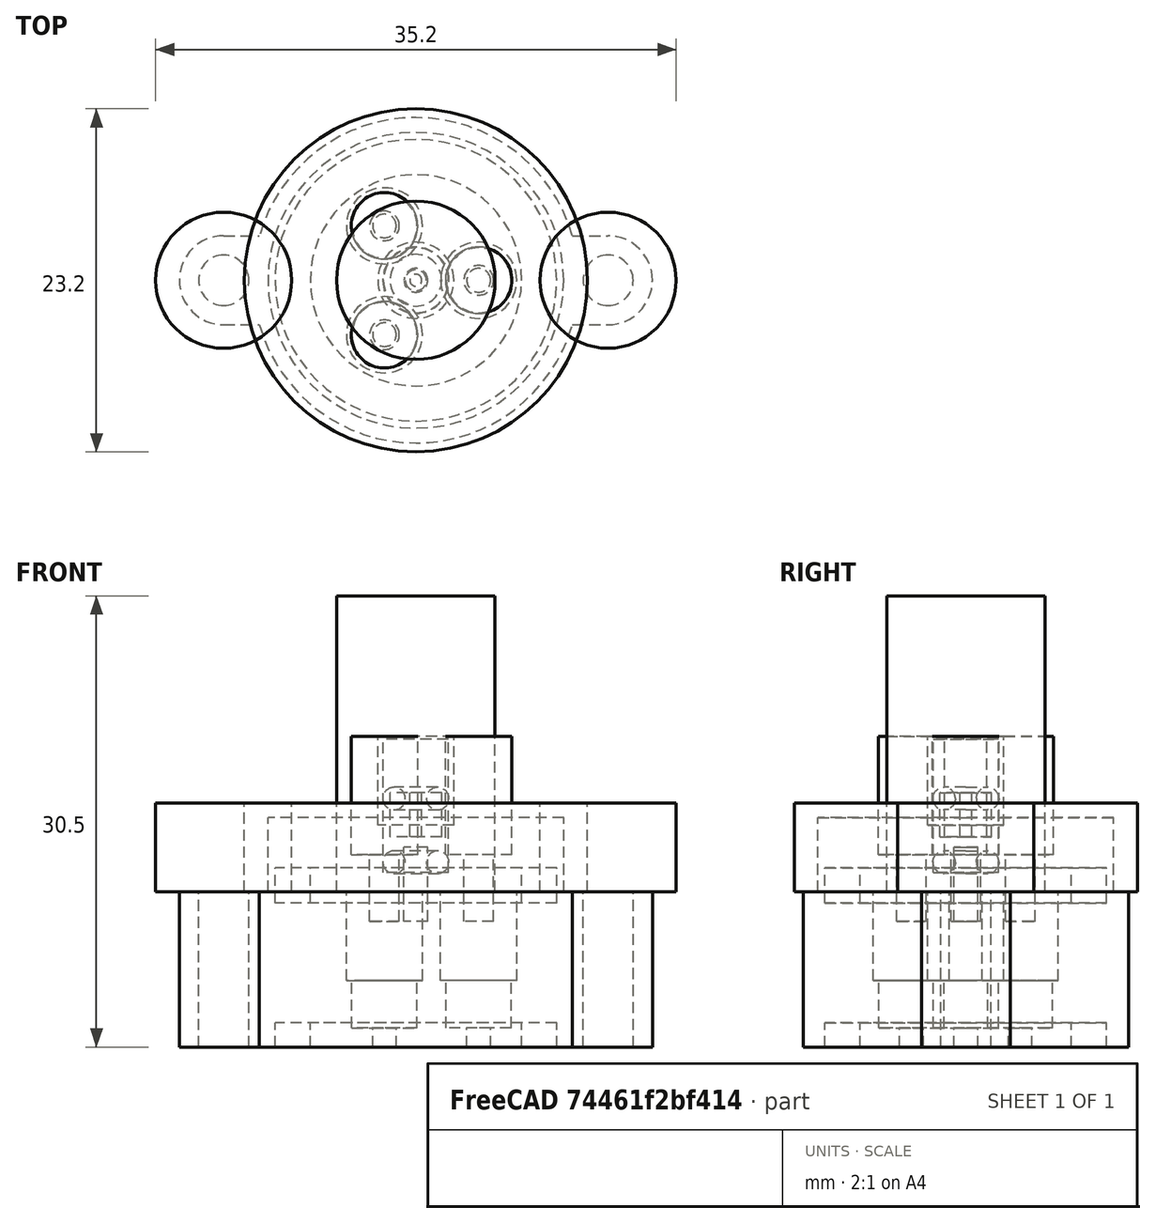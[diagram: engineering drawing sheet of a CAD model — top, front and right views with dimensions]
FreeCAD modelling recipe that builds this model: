
FCSTD DOCUMENT  (FreeCAD 0.17R13509 (Git))
Label: ceramic_wire_feedthroughs_insert
License: All rights reserved
LicenseURL: http://en.wikipedia.org/wiki/All_rights_reserved
objects: Part::Cylinder×45, Part::MultiFuse×10, Part::Cut×8, Part::Box×6, Part::FeaturePython×4, Part::Feature×2, App::FeaturePython×1
note: 75 computed .brp shape members not serialized (recipe doc carries the construction recipe); baked Part::Feature solids carry a one-line shape summary decoded from their .brp

FEATURE [Part::Cylinder] Cylinder155  label="Cylinder009"
  Angle = 360
  AttacherType = Attacher::AttachEngine3D
  Height = 2.38125
  Radius = 9.525
  expr: Radius = 3 / 4 * 25.399999999999999 / 2
  expr: Height = 3 / 32 * 25.399999999999999
FEATURE [Part::Cylinder] Cylinder154  label="Cylinder008"
  Angle = 360
  AttacherType = Attacher::AttachEngine3D
  Height = 2.38125
  Radius = 7.14375
  expr: Radius = 9 / 16 * 25.399999999999999 / 2
  expr: Height = 3 / 32 * 25.399999999999999
FEATURE [Part::Feature] Part__Feature001  label="TopOring"
  Placement = pos=(0,0,6.3) rot=(0,0,1;0rad)
  shape: bbox 4.839 x 4.839 x 1.524 mm, 4 faces (baked)
FEATURE [Part::Feature] Part__Feature002  label="BottomOring"
  Placement = pos=(0,0,2) rot=(0,0,1;0rad)
  shape: bbox 4.839 x 4.839 x 1.524 mm, 4 faces (baked)
FEATURE [Part::Cylinder] Cylinder153  label="Body"
  Angle = 360
  AttacherType = Attacher::AttachEngine3D
  Height = 5
  Radius = 10
FEATURE [Part::Cut] Cut019  label="Oring"
  Base = -> Cylinder155
  Placement = pos=(0,0,-0.75) rot=(0,0,1;0rad)
  Tool = -> Cylinder154
FEATURE [Part::Cylinder] Cylinder147  label="ThreadedSection"
  Angle = 360
  AttacherType = Attacher::AttachEngine3D
  Height = 1
  Placement = pos=(0,0,4.5) rot=(0,0,1;0rad)
  Radius = 1
FEATURE [Part::Cylinder] Cylinder149  label="FTBead"
  Angle = 360
  AttacherType = Attacher::AttachEngine3D
  Height = 3
  Placement = pos=(0,0,2.7) rot=(0,0,1;0rad)
  Radius = 1.75
  expr: Radius = 3.5 / 2
FEATURE [Part::Cylinder] Cylinder152  label="RFFeeds005"
  Angle = 360
  AttacherType = Attacher::AttachEngine3D
  Height = 20
  Radius = 5.35813
  expr: Placement.Base.x = 0
FEATURE [Part::Cylinder] Cylinder156  label="BottomWireOutlet"
  Angle = 360
  AttacherType = Attacher::AttachEngine3D
  Height = 5
  Placement = pos=(0,0,-2) rot=(0,0,1;0rad)
  Radius = 1
FEATURE [Part::Cylinder] Cylinder157  label="SealSubtraction"
  Angle = 360
  AttacherType = Attacher::AttachEngine3D
  Height = 8
  Placement = pos=(0,0,2.5) rot=(0,0,1;0rad)
  Radius = 2.25
FEATURE [Part::MultiFuse] Fusion
  Placement = pos=(4.25,0,0) rot=(0,0,1;0rad)
  Shapes = -> [Cylinder147,Cylinder157,Cylinder156]
FEATURE [Part::FeaturePython] Array  label="SealArray"  # Draft array (typed FeaturePython)
  Angle = 360
  ArrayType = 1
  Axis = (0,0,1)
  Base = -> Fusion
  Center = (0,0,0)
  Fuse = false
  IntervalAxis = (0,0,0)
  IntervalX = (1,0,0)
  IntervalY = (0,1,0)
  IntervalZ = (0,0,0)
  NumberPolar = 3
  NumberX = 2
  NumberY = 2
  NumberZ = 1
FEATURE [Part::Cylinder] Cylinder159  label="FTBeadHole"
  Angle = 360
  AttacherType = Attacher::AttachEngine3D
  Height = 17
  Radius = 0.405
  expr: Radius = 0.81000000000000005 / 2
FEATURE [Part::Cut] Cut020
  Base = -> Cylinder149
  Placement = pos=(0,0,1) rot=(0,0,1;0rad)
  Tool = -> Cylinder159
FEATURE [Part::Cylinder] Cylinder160  label="Cylinder010"
  Angle = 360
  AttacherType = Attacher::AttachEngine3D
  Height = 2.38125
  Radius = 9.525
  expr: Radius = 3 / 4 * 25.399999999999999 / 2
  expr: Height = 3 / 32 * 25.399999999999999
FEATURE [Part::Cylinder] Cylinder161  label="WireFeedsMount003"
  Angle = 360
  AttacherType = Attacher::AttachEngine3D
  Height = 11
  Placement = pos=(-13,0,0) rot=(0,0,1;0rad)
  Radius = 1.7
FEATURE [Part::Cylinder] Cylinder162  label="ThreadedSection001"
  Angle = 360
  AttacherType = Attacher::AttachEngine3D
  Height = 6
  Placement = pos=(0,0,4.5) rot=(0,0,1;0rad)
  Radius = 2.575
  expr: Radius = 5.1500000000000004 / 2
FEATURE [Part::Cylinder] Cylinder163  label="Cylinder011"
  Angle = 360
  AttacherType = Attacher::AttachEngine3D
  Height = 2.38125
  Radius = 7.14375
  expr: Radius = 9 / 16 * 25.399999999999999 / 2
  expr: Height = 3 / 32 * 25.399999999999999
FEATURE [Part::Cut] Cut022  label="Oring001"
  Base = -> Cylinder160
  Placement = pos=(0,0,-0.75) rot=(0,0,1;0rad)
  Tool = -> Cylinder163
FEATURE [Part::Cylinder] Cylinder164  label="Body001"
  Angle = 360
  AttacherType = Attacher::AttachEngine3D
  Height = 10.5
  Radius = 11
FEATURE [Part::Cylinder] Cylinder165  label="WireFeedsMount004"
  Angle = 360
  AttacherType = Attacher::AttachEngine3D
  Height = 11
  Placement = pos=(13,0,0) rot=(0,0,1;0rad)
  Radius = 1.7
FEATURE [Part::Cylinder] Cylinder166  label="BottomWireOutlet001"
  Angle = 360
  AttacherType = Attacher::AttachEngine3D
  Height = 5
  Placement = pos=(0,0,-2) rot=(0,0,1;0rad)
  Radius = 0.8
FEATURE [Part::Cylinder] Cylinder167  label="SealSubtraction001"
  Angle = 360
  AttacherType = Attacher::AttachEngine3D
  Height = 9
  Placement = pos=(0,0,1.3) rot=(0,0,1;0rad)
  Radius = 2.2
FEATURE [Part::Box] Box002  label="MountCube003"
  AttacherType = Attacher::AttachEngine3D
  Height = 10.5
  Length = 3
  Placement = pos=(10,-3,0) rot=(0,0,1;0rad)
  Width = 6
FEATURE [Part::Box] Box003  label="MountCube004"
  AttacherType = Attacher::AttachEngine3D
  Height = 10.5
  Length = 3
  Placement = pos=(-13,-3,0) rot=(0,0,1;0rad)
  Width = 6
FEATURE [Part::MultiFuse] Fusion004
  Placement = pos=(4.25,0,0) rot=(0,0,1;0rad)
  Shapes = -> [Cylinder162,Cylinder167,Cylinder166]
FEATURE [Part::Cylinder] Cylinder168  label="MountFlange003"
  Angle = 360
  AttacherType = Attacher::AttachEngine3D
  Height = 10.5
  Placement = pos=(-13,0,0) rot=(0,0,1;0rad)
  Radius = 3
FEATURE [Part::Cylinder] Cylinder169  label="MountFlange004"
  Angle = 360
  AttacherType = Attacher::AttachEngine3D
  Height = 10.5
  Placement = pos=(13,0,0) rot=(0,0,1;0rad)
  Radius = 3
FEATURE [Part::MultiFuse] Fusion003
  Shapes = -> [Cylinder169,Box002,Box003,Cylinder168,Cylinder164]
FEATURE [Part::FeaturePython] Array001  label="SealArray001"  # Draft array (typed FeaturePython)
  Angle = 360
  ArrayType = 1
  Axis = (0,0,1)
  Base = -> Fusion004
  Center = (0,0,0)
  Fuse = false
  IntervalAxis = (0,0,0)
  IntervalX = (1,0,0)
  IntervalY = (0,1,0)
  IntervalZ = (0,0,0)
  NumberPolar = 3
  NumberX = 2
  NumberY = 2
  NumberZ = 1
FEATURE [Part::MultiFuse] Fusion005
  Shapes = -> [Cylinder165,Cylinder161,Cut022,Array001]
FEATURE [Part::Cut] Cut021
  Base = -> Fusion003
  Placement = pos=(0,0,-10.5) rot=(0,0,1;0rad)
  Tool = -> Fusion005
FEATURE [Part::Cylinder] Cylinder170  label="Cylinder012"
  Angle = 360
  AttacherType = Attacher::AttachEngine3D
  Height = 2.38125
  Radius = 9.525
  expr: Radius = 3 / 4 * 25.399999999999999 / 2
  expr: Height = 3 / 32 * 25.399999999999999
FEATURE [Part::Cylinder] Cylinder171  label="WireFeedsMount005"
  Angle = 360
  AttacherType = Attacher::AttachEngine3D
  Height = 11
  Placement = pos=(-13,0,0) rot=(0,0,1;0rad)
  Radius = 1.7
FEATURE [Part::Cylinder] Cylinder172  label="ThreadedSection002"
  Angle = 360
  AttacherType = Attacher::AttachEngine3D
  Height = 6
  Placement = pos=(0,0,4.5) rot=(0,0,1;0rad)
  Radius = 2.575
  expr: Radius = 5.1500000000000004 / 2
FEATURE [Part::Cylinder] Cylinder173  label="Cylinder013"
  Angle = 360
  AttacherType = Attacher::AttachEngine3D
  Height = 2.38125
  Radius = 7.14375
  expr: Radius = 9 / 16 * 25.399999999999999 / 2
  expr: Height = 3 / 32 * 25.399999999999999
FEATURE [Part::Cut] Cut024  label="Oring002"
  Base = -> Cylinder170
  Placement = pos=(0,0,-0.75) rot=(0,0,1;0rad)
  Tool = -> Cylinder173
FEATURE [Part::Cylinder] Cylinder174  label="Body002"
  Angle = 360
  AttacherType = Attacher::AttachEngine3D
  Height = 10.5
  Radius = 11
FEATURE [Part::Cylinder] Cylinder175  label="WireFeedsMount006"
  Angle = 360
  AttacherType = Attacher::AttachEngine3D
  Height = 11
  Placement = pos=(13,0,0) rot=(0,0,1;0rad)
  Radius = 1.7
FEATURE [Part::Cylinder] Cylinder176  label="BottomWireOutlet002"
  Angle = 360
  AttacherType = Attacher::AttachEngine3D
  Height = 5
  Placement = pos=(0,0,-2) rot=(0,0,1;0rad)
  Radius = 0.8
FEATURE [Part::Cylinder] Cylinder177  label="SealSubtraction002"
  Angle = 360
  AttacherType = Attacher::AttachEngine3D
  Height = 9
  Placement = pos=(0,0,1.3) rot=(0,0,1;0rad)
  Radius = 2.2
FEATURE [Part::Box] Box004  label="MountCube005"
  AttacherType = Attacher::AttachEngine3D
  Height = 10.5
  Length = 3
  Placement = pos=(10,-3,0) rot=(0,0,1;0rad)
  Width = 6
FEATURE [App::FeaturePython] SetupSheet002  # Path/CAM operation (typed FeaturePython)
  ClearanceHeightExpression = StartDepth+SetupSheet.ClearanceHeightOffset
  ClearanceHeightOffset = 5
  FinalDepthExpression = OpFinalDepth
  HorizRapid = 0
  SafeHeightExpression = StartDepth+SetupSheet.SafeHeightOffset
  SafeHeightOffset = 3
  StartDepthExpression = OpStartDepth
  StepDownExpression = OpToolDiameter
  VertRapid = 0
FEATURE [Part::Box] Box005  label="MountCube006"
  AttacherType = Attacher::AttachEngine3D
  Height = 10.5
  Length = 3
  Placement = pos=(-13,-3,0) rot=(0,0,1;0rad)
  Width = 6
FEATURE [Part::MultiFuse] Fusion007
  Placement = pos=(4.25,0,0) rot=(0,0,1;0rad)
  Shapes = -> [Cylinder172,Cylinder177,Cylinder176]
FEATURE [Part::Cylinder] Cylinder178  label="MountFlange005"
  Angle = 360
  AttacherType = Attacher::AttachEngine3D
  Height = 10.5
  Placement = pos=(-13,0,0) rot=(0,0,1;0rad)
  Radius = 3
FEATURE [Part::Cylinder] Cylinder179  label="MountFlange006"
  Angle = 360
  AttacherType = Attacher::AttachEngine3D
  Height = 10.5
  Placement = pos=(13,0,0) rot=(0,0,1;0rad)
  Radius = 3
FEATURE [Part::MultiFuse] Fusion006
  Shapes = -> [Cylinder179,Box004,Box005,Cylinder178,Cylinder174]
FEATURE [Part::FeaturePython] Array002  label="SealArray002"  # Draft array (typed FeaturePython)
  Angle = 360
  ArrayType = 1
  Axis = (0,0,1)
  Base = -> Fusion007
  Center = (0,0,0)
  Fuse = false
  IntervalAxis = (0,0,0)
  IntervalX = (1,0,0)
  IntervalY = (0,1,0)
  IntervalZ = (0,0,0)
  NumberPolar = 3
  NumberX = 2
  NumberY = 2
  NumberZ = 1
FEATURE [Part::MultiFuse] Fusion008
  Shapes = -> [Cylinder175,Cylinder171,Cut024,Array002]
FEATURE [Part::Cut] Cut023
  Base = -> Fusion006
  Placement = pos=(0,0,-10.5) rot=(0,0,1;0rad)
  Tool = -> Fusion008
FEATURE [Part::Cylinder] Cylinder180  label="Cylinder014"
  Angle = 360
  AttacherType = Attacher::AttachEngine3D
  Height = 2.38125
  Radius = 7.14375
  expr: Radius = 9 / 16 * 25.399999999999999 / 2
  expr: Height = 3 / 32 * 25.399999999999999
FEATURE [Part::Cylinder] Cylinder181  label="MountFlange007"
  Angle = 360
  AttacherType = Attacher::AttachEngine3D
  Height = 10.5
  Placement = pos=(-13,0,0) rot=(0,0,1;0rad)
  Radius = 3
FEATURE [Part::Box] Box006  label="MountCube007"
  AttacherType = Attacher::AttachEngine3D
  Height = 10.5
  Length = 3
  Placement = pos=(-13,-3,0) rot=(0,0,1;0rad)
  Width = 6
FEATURE [Part::Cylinder] Cylinder182  label="WireFeedsMount007"
  Angle = 360
  AttacherType = Attacher::AttachEngine3D
  Height = 11
  Placement = pos=(13,0,0) rot=(0,0,1;0rad)
  Radius = 1.7
FEATURE [Part::Box] Box007  label="MountCube008"
  AttacherType = Attacher::AttachEngine3D
  Height = 10.5
  Length = 3
  Placement = pos=(10,-3,0) rot=(0,0,1;0rad)
  Width = 6
FEATURE [Part::Cylinder] Cylinder183  label="WireFeedsMount008"
  Angle = 360
  AttacherType = Attacher::AttachEngine3D
  Height = 11
  Placement = pos=(-13,0,0) rot=(0,0,1;0rad)
  Radius = 1.7
FEATURE [Part::Cylinder] Cylinder184  label="Body003"
  Angle = 360
  AttacherType = Attacher::AttachEngine3D
  Height = 10.5
  Radius = 11
FEATURE [Part::Cylinder] Cylinder185  label="MountFlange008"
  Angle = 360
  AttacherType = Attacher::AttachEngine3D
  Height = 10.5
  Placement = pos=(13,0,0) rot=(0,0,1;0rad)
  Radius = 3
FEATURE [Part::Cylinder] Cylinder186  label="BottomWireOutlet003"
  Angle = 360
  AttacherType = Attacher::AttachEngine3D
  Height = 5
  Placement = pos=(0,0,-2) rot=(0,0,1;0rad)
  Radius = 0.8
FEATURE [Part::MultiFuse] Fusion011
  Shapes = -> [Cylinder185,Box007,Box006,Cylinder181,Cylinder184]
FEATURE [Part::Cylinder] Cylinder187  label="ThreadedSection003"
  Angle = 360
  AttacherType = Attacher::AttachEngine3D
  Height = 6
  Placement = pos=(0,0,4.5) rot=(0,0,1;0rad)
  Radius = 2.575
  expr: Radius = 5.1500000000000004 / 2
FEATURE [Part::Cylinder] Cylinder188  label="Cylinder015"
  Angle = 360
  AttacherType = Attacher::AttachEngine3D
  Height = 2.38125
  Radius = 9.525
  expr: Radius = 3 / 4 * 25.399999999999999 / 2
  expr: Height = 3 / 32 * 25.399999999999999
FEATURE [Part::Cut] Cut025  label="Oring003"
  Base = -> Cylinder188
  Placement = pos=(0,0,-0.75) rot=(0,0,1;0rad)
  Tool = -> Cylinder180
FEATURE [Part::Cylinder] Cylinder189  label="SealSubtraction003"
  Angle = 360
  AttacherType = Attacher::AttachEngine3D
  Height = 9
  Placement = pos=(0,0,1.3) rot=(0,0,1;0rad)
  Radius = 2.2
FEATURE [Part::MultiFuse] Fusion009
  Placement = pos=(4.25,0,0) rot=(0,0,1;0rad)
  Shapes = -> [Cylinder187,Cylinder189,Cylinder186]
FEATURE [Part::FeaturePython] Array003  label="SealArray003"  # Draft array (typed FeaturePython)
  Angle = 360
  ArrayType = 1
  Axis = (0,0,1)
  Base = -> Fusion009
  Center = (0,0,0)
  Fuse = false
  IntervalAxis = (0,0,0)
  IntervalX = (1,0,0)
  IntervalY = (0,1,0)
  IntervalZ = (0,0,0)
  NumberPolar = 3
  NumberX = 2
  NumberY = 2
  NumberZ = 1
FEATURE [Part::MultiFuse] Fusion010
  Shapes = -> [Cylinder182,Cylinder183,Cut025,Array003]
FEATURE [Part::Cut] Cut026
  Base = -> Fusion011
  Placement = pos=(0,0,-10.5) rot=(0,0,1;0rad)
  Tool = -> Fusion010
FEATURE [Part::Cylinder] Cylinder192  label="ThreadedSection004"
  Angle = 360
  AttacherType = Attacher::AttachEngine3D
  Height = 6
  Placement = pos=(0,0,4.5) rot=(0,0,1;0rad)
  Radius = 2.575
  expr: Radius = 5.1500000000000004 / 2
FEATURE [Part::Cylinder] Cylinder196  label="BottomWireOutlet004"
  Angle = 360
  AttacherType = Attacher::AttachEngine3D
  Height = 5
  Placement = pos=(0,0,-2) rot=(0,0,1;0rad)
  Radius = 0.8
FEATURE [Part::Cylinder] Cylinder197  label="SealSubtraction004"
  Angle = 360
  AttacherType = Attacher::AttachEngine3D
  Height = 9
  Placement = pos=(0,0,1.3) rot=(0,0,1;0rad)
  Radius = 2.2
FEATURE [Part::Cylinder] Cylinder198  label="Cylinder"
  Angle = 360
  AttacherType = Attacher::AttachEngine3D
  Height = 6
  Radius = 11.6
FEATURE [Part::Cylinder] Cylinder199  label="Cylinder016"
  Angle = 360
  AttacherType = Attacher::AttachEngine3D
  Height = 6
  Placement = pos=(-13,0,0) rot=(0,0,1;0rad)
  Radius = 4.6
FEATURE [Part::Cylinder] Cylinder200  label="Cylinder017"
  Angle = 360
  AttacherType = Attacher::AttachEngine3D
  Height = 6
  Placement = pos=(13,0,0) rot=(0,0,1;0rad)
  Radius = 4.6
